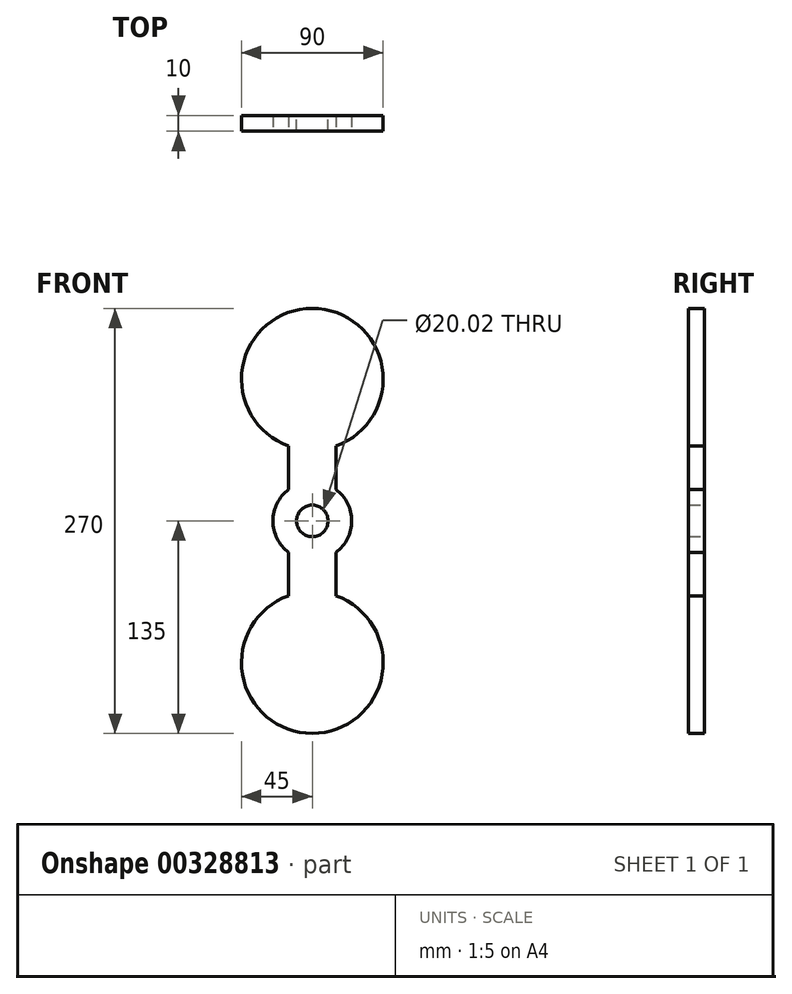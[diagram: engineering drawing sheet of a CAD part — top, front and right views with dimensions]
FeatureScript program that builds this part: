
annotation { "Feature Type Name" : "Feature", "Feature Type Description" : "" }
export const myFeature = defineFeature(function(context is Context, id is Id, definition is map)
    precondition{}
    {
        {
            var Q0;
            Q0=qCreatedBy(makeId("Front.planeOp"),FACE);
            var sketch = newSketch(context, id + "F0", { "sketchPlane" : qUnion([Q0])});
            skLineSegment(sketch, "E0.bottom", {"start": v(-15, 90) * mm, "end": v(15, 90) * mm});
            skLineSegment(sketch, "E0.top", {"start": v(-15, -90) * mm, "end": v(15, -90) * mm});
            skLineSegment(sketch, "E0.left", {"start": v(-15, 90) * mm, "end": v(-15, -90) * mm});
            skLineSegment(sketch, "E0.right", {"start": v(15, 90) * mm, "end": v(15, -90) * mm});
            skPoint(sketch, "E0.middle", {"position": v(0, 0) * mm});
            skCircle(sketch, "E1", {"center": v(0, 0) * mm, "radius": 10 * mm});
            skSolve(sketch);
        }
        {
            var Q0;
            Q0 = qSketchRegion(id + "F0", true);
            extrude(context, id + "F1", {"entities" : qUnion([Q0]), "depth" : 10 * mm});
        }
        {
            var Q0;
            Q0=makeQuery(id+"F1.opExtrude","CAP_FACE",FACE,{"disambiguationData":[OSD([sQuery(id+"F0.wireOp",EDGE,"E0.bottom"),sQuery(id+"F0.wireOp",EDGE,"E0.top"),sQuery(id+"F0.wireOp",EDGE,"E0.left"),sQuery(id+"F0.wireOp",EDGE,"E0.right"),sQuery(id+"F0.wireOp",EDGE,"E1")])],"isStart":false});
            var sketch = newSketch(context, id + "F2", { "sketchPlane" : qUnion([Q0])});
            skCircle(sketch, "E2", {"center": v(0, 0) * mm, "radius": 25 * mm});
            skCircle(sketch, "E3", {"center": v(0, 0) * mm, "radius": 10 * mm});
            skSolve(sketch);
        }
        {
            var Q0;
            {var subQ0=sQuery(id+"F2.wireOp",EDGE,"E2");var subQ1=makeQuery(id+"F1.opExtrude","CAP_EDGE",EDGE,{"disambiguationData":[OSD([sQuery(id+"F0.wireOp",EDGE,"E0.left")])],"isStart":false});var subQ2=makeQuery(id+"F2.imprint","INTERSECT",VERTEX,{"disambiguationData":[OD(0.0)],"derivedFrom":[subQ1,subQ0]});Q0=makeQuery(id+"F2.imprint","IMPRINT",FACE,{"disambiguationData":[TD([[makeQuery(id+"F2.imprint","IMPRINT",EDGE,{"disambiguationData":[TD([[subQ2,-1.0]])],"derivedFrom":subQ0}),1.0]])]});}
            var Q1;
            Q1=makeQuery(id+"F2.imprint","IMPRINT",FACE,{"disambiguationData":[TD([[makeQuery(id+"F2.imprint","IMPRINT",EDGE,{"derivedFrom":sQuery(id+"F2.wireOp",EDGE,"E3")}),-1.0]])]});
            var Q2;
            {var subQ0=sQuery(id+"F2.wireOp",EDGE,"E2");var subQ1=makeQuery(id+"F1.opExtrude","CAP_EDGE",EDGE,{"disambiguationData":[OSD([sQuery(id+"F0.wireOp",EDGE,"E0.right")])],"isStart":false});var subQ2=makeQuery(id+"F2.imprint","INTERSECT",VERTEX,{"disambiguationData":[OD(0.0)],"derivedFrom":[subQ1,subQ0]});Q2=makeQuery(id+"F2.imprint","IMPRINT",FACE,{"disambiguationData":[TD([[makeQuery(id+"F2.imprint","IMPRINT",EDGE,{"disambiguationData":[TD([[subQ2,1.0]])],"derivedFrom":subQ0}),1.0]])]});}
            extrude(context, id + "F3", {"entities" : qUnion([Q0, Q1, Q2]), "operationType" : NewBodyOperationType.ADD, "oppositeDirection" : true, "depth" : 10 * mm});
        }
        {
            var Q0;
            Q0=makeQuery(id+"F3.boolean.opBoolean","MERGE",FACE,{"derivedFrom":[makeQuery(id+"F1.opExtrude","CAP_FACE",FACE,{"disambiguationData":[OSD([sQuery(id+"F0.wireOp",EDGE,"E0.bottom"),sQuery(id+"F0.wireOp",EDGE,"E0.top"),sQuery(id+"F0.wireOp",EDGE,"E0.left"),sQuery(id+"F0.wireOp",EDGE,"E0.right"),sQuery(id+"F0.wireOp",EDGE,"E1")])],"isStart":false}),makeQuery(id+"F3.opExtrude","CAP_FACE",FACE,{"disambiguationData":[OSD([sQuery(id+"F2.wireOp",EDGE,"E2"),sQuery(id+"F2.wireOp",EDGE,"E3")])],"isStart":true})]});
            var sketch = newSketch(context, id + "F4", { "sketchPlane" : qUnion([Q0])});
            skCircle(sketch, "E4", {"center": v(0, 90) * mm, "radius": 45 * mm});
            skCircle(sketch, "E5", {"center": v(0, -90) * mm, "radius": 45 * mm});
            skSolve(sketch);
        }
        {
            var Q0;
            {var subQ4=sQuery(id+"F0.wireOp",EDGE,"E0.top");var subQ13=makeQuery(id+"F1.opExtrude","CAP_EDGE",EDGE,{"disambiguationData":[OSD([subQ4])],"isStart":false});Q0=makeQuery(id+"F4.imprint","IMPRINT",FACE,{"disambiguationData":[TD([[makeQuery(id+"F4.imprint","IMPRINT",EDGE,{"derivedFrom":subQ13}),-1.0]])]});}
            var Q1;
            {var subQ4=sQuery(id+"F0.wireOp",EDGE,"E0.top");var subQ13=makeQuery(id+"F1.opExtrude","CAP_EDGE",EDGE,{"disambiguationData":[OSD([subQ4])],"isStart":false});Q1=makeQuery(id+"F4.imprint","IMPRINT",FACE,{"disambiguationData":[TD([[makeQuery(id+"F4.imprint","IMPRINT",EDGE,{"derivedFrom":subQ13}),1.0]])]});}
            var Q2;
            {var subQ5=sQuery(id+"F0.wireOp",EDGE,"E0.bottom");var subQ13=makeQuery(id+"F1.opExtrude","CAP_EDGE",EDGE,{"disambiguationData":[OSD([subQ5])],"isStart":false});Q2=makeQuery(id+"F4.imprint","IMPRINT",FACE,{"disambiguationData":[TD([[makeQuery(id+"F4.imprint","IMPRINT",EDGE,{"derivedFrom":subQ13}),1.0]])]});}
            var Q3;
            {var subQ5=sQuery(id+"F0.wireOp",EDGE,"E0.bottom");var subQ13=makeQuery(id+"F1.opExtrude","CAP_EDGE",EDGE,{"disambiguationData":[OSD([subQ5])],"isStart":false});Q3=makeQuery(id+"F4.imprint","IMPRINT",FACE,{"disambiguationData":[TD([[makeQuery(id+"F4.imprint","IMPRINT",EDGE,{"derivedFrom":subQ13}),-1.0]])]});}
            extrude(context, id + "F5", {"entities" : qUnion([Q0, Q1, Q2, Q3]), "operationType" : NewBodyOperationType.ADD, "oppositeDirection" : true, "depth" : 10 * mm});
        }
    });
